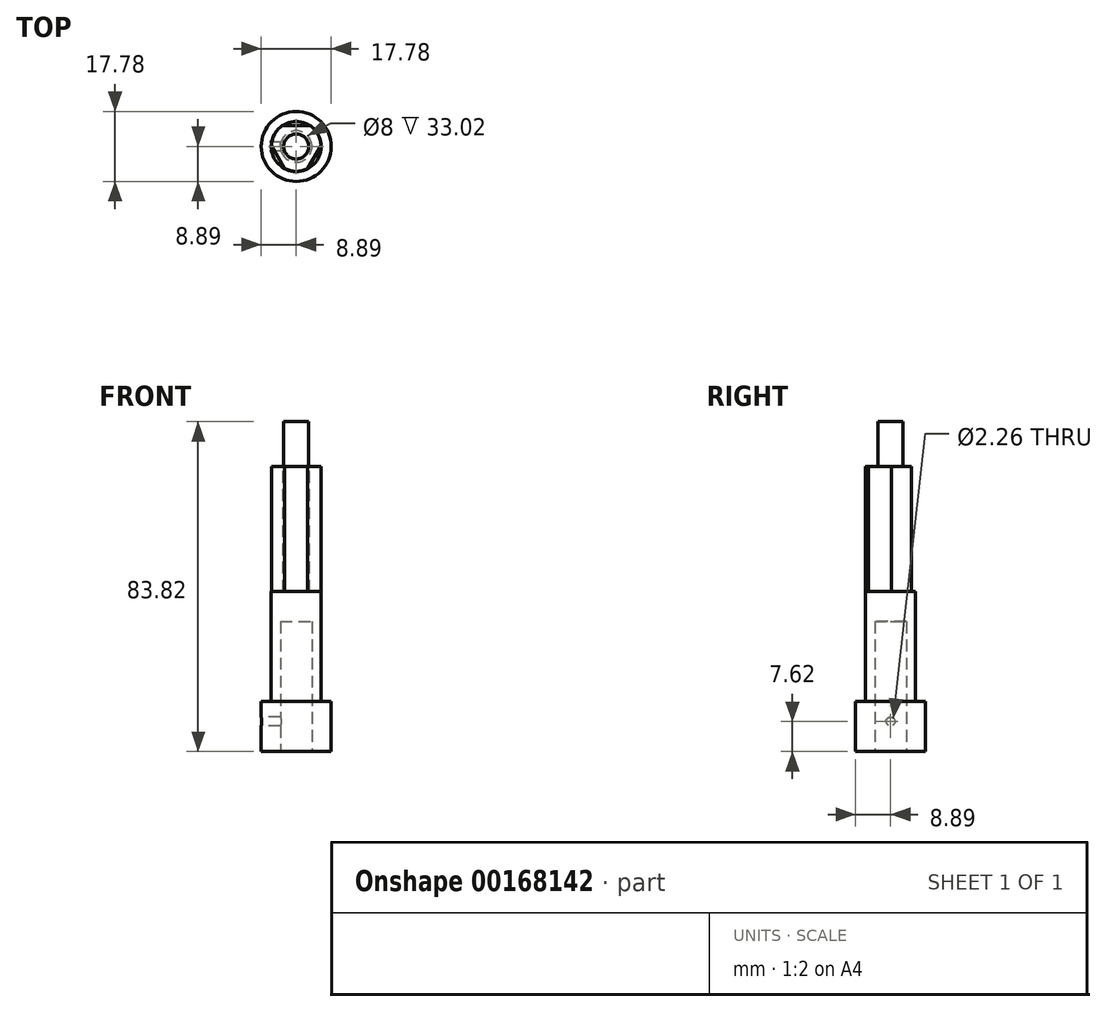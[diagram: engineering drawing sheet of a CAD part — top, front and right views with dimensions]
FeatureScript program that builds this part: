
annotation { "Feature Type Name" : "Feature", "Feature Type Description" : "" }
export const myFeature = defineFeature(function(context is Context, id is Id, definition is map)
    precondition{}
    {
        {
            var Q0;
            Q0=qCreatedBy(makeId("Top.planeOp"),FACE);
            var sketch = newSketch(context, id + "F0", { "sketchPlane" : qUnion([Q0])});
            skCircle(sketch, "E0", {"center": v(0, 0) * mm, "radius": 8.9 * mm});
            skSolve(sketch);
        }
        {
            var Q0;
            Q0=makeQuery(id+"F0.imprint","IMPRINT",FACE,{"disambiguationData":[TD([[makeQuery(id+"F0.imprint","IMPRINT",EDGE,{"derivedFrom":sQuery(id+"F0.wireOp",EDGE,"E0")}),1.0]])]});
            extrude(context, id + "F1", {"entities" : qUnion([Q0]), "depth" : 12.7 * mm});
        }
        {
            var Q0;
            Q0=makeQuery(id+"F1.opExtrude","CAP_FACE",FACE,{"disambiguationData":[OSD([sQuery(id+"F0.wireOp",EDGE,"E0")])],"isStart":false});
            var sketch = newSketch(context, id + "F2", { "sketchPlane" : qUnion([Q0])});
            skCircle(sketch, "E1", {"center": v(0, 0) * mm, "radius": 6.35 * mm});
            skSolve(sketch);
        }
        {
            var Q0;
            Q0=qSketchRegion(id+"F2",true);
            extrude(context, id + "F3", {"entities" : qUnion([Q0]), "operationType" : NewBodyOperationType.ADD, "depth" : 27.94 * mm});
        }
        {
            var Q0;
            Q0=makeQuery(id+"F3.opExtrude","CAP_FACE",FACE,{"disambiguationData":[OSD([sQuery(id+"F2.wireOp",EDGE,"E1")])],"isStart":false});
            var sketch = newSketch(context, id + "F4", { "sketchPlane" : qUnion([Q0])});
            skCircle(sketch, "E2.cCircle", {"center": v(0, 0) * mm, "radius": 5.33 * mm, "construction": true});
            skLineSegment(sketch, "E2.0", {"start": v(9.24, 5.33) * mm, "end": v(0, -10.67) * mm});
            skLineSegment(sketch, "E2.1", {"start": v(0, -10.67) * mm, "end": v(-9.24, 5.33) * mm});
            skLineSegment(sketch, "E2.2", {"start": v(-9.24, 5.33) * mm, "end": v(9.24, 5.33) * mm});
            skPoint(sketch, "E2.0.midPoint", {"position": v(4.62, -2.67) * mm});
            skSolve(sketch);
        }
        {
            var Q0;
            Q0=qSketchRegion(id+"F4",true);
            extrude(context, id + "F5", {"entities" : qUnion([Q0]), "operationType" : NewBodyOperationType.ADD, "depth" : 43.18 * mm});
        }
        {
            var Q0;
            Q0=makeQuery(id+"F5.opExtrude","CAP_FACE",FACE,{"disambiguationData":[OSD([sQuery(id+"F4.wireOp",EDGE,"E2.0"),sQuery(id+"F4.wireOp",EDGE,"E2.1"),sQuery(id+"F4.wireOp",EDGE,"E2.2")])],"isStart":false});
            var sketch = newSketch(context, id + "F6", { "sketchPlane" : qUnion([Q0])});
            skCircle(sketch, "E3", {"center": v(0, 0) * mm, "radius": 6.32 * mm});
            skCircle(sketch, "E4", {"center": v(0, 0) * mm, "radius": 20.25 * mm});
            skSolve(sketch);
        }
        {
            var Q0;
            Q0=qSketchRegion(id+"F6",true);
            var Q1;
            {var subQ0=sQuery(id+"F2.wireOp",EDGE,"E1");var subQ1=sQuery(id+"F4.wireOp",EDGE,"E2.0");Q1=makeQuery(id+"F5.boolean.opBoolean","SPLIT",FACE,{"disambiguationData":[TD([makeQuery(id+"F5.opExtrude","SWEPT_FACE",FACE,{"disambiguationData":[OSD([subQ1])]})])],"derivedFrom":makeQuery(id+"F3.opExtrude","CAP_FACE",FACE,{"disambiguationData":[OSD([subQ0])],"isStart":false})});}
            extrude(context, id + "F7", {"entities" : qUnion([Q0]), "operationType" : NewBodyOperationType.REMOVE, "endBound" : BoundingType.UP_TO_SURFACE, "oppositeDirection" : true, "endBoundEntityFace" : qUnion([Q1]), "depth" : 25.4 * mm});
        }
        {
            var Q0;
            Q0=makeQuery(id+"F1.opExtrude","CAP_FACE",FACE,{"disambiguationData":[OSD([sQuery(id+"F0.wireOp",EDGE,"E0")])],"isStart":true});
            var sketch = newSketch(context, id + "F8", { "sketchPlane" : qUnion([Q0])});
            skCircle(sketch, "E5", {"center": v(0, 0) * mm, "radius": 4 * mm});
            skSolve(sketch);
        }
        {
            var Q0;
            Q0=makeQuery(id+"F8.imprint","IMPRINT",FACE,{"disambiguationData":[TD([[makeQuery(id+"F8.imprint","IMPRINT",EDGE,{"derivedFrom":sQuery(id+"F8.wireOp",EDGE,"E5")}),1.0]])]});
            extrude(context, id + "F9", {"entities" : qUnion([Q0]), "operationType" : NewBodyOperationType.REMOVE, "oppositeDirection" : true, "depth" : 33.02 * mm});
        }
        {
            var Q0;
            Q0=makeQuery(id+"F1.opExtrude","CAP_FACE",FACE,{"disambiguationData":[OSD([sQuery(id+"F0.wireOp",EDGE,"E0")])],"isStart":false});
            var sketch = newSketch(context, id + "F10", { "sketchPlane" : qUnion([Q0])});
            skCircle(sketch, "E6.0", {"center": v(0, 0) * mm, "radius": 8.9 * mm, "construction": true});
            skPoint(sketch, "E7", {"position": v(-8.9, 0) * mm});
            skSolve(sketch);
        }
        {
            var Q0;
            Q0=sQuery(id+"F10.wireOp",VERTEX,"E7");
            var Q1;
            Q1=qCreatedBy(makeId("Right.planeOp"),FACE);
            cPlane(context, id + "F11", {"entities" : qUnion([Q0, Q1]), "cplaneType" : CPlaneType.PLANE_POINT, "offset" : 25.4 * mm, "width" : 152.4 * mm, "height" : 152.4 * mm});
        }
        {
            var Q0;
            Q0=qCreatedBy(id+"F11.planeOp",FACE);
            var sketch = newSketch(context, id + "F12", { "sketchPlane" : qUnion([Q0])});
            skLineSegment(sketch, "E8", {"start": v(0, 0) * mm, "end": v(0, 7.62) * mm, "construction": true});
            skPoint(sketch, "E9", {"position": v(0, 7.62) * mm});
            skSolve(sketch);
        }
        {
            var Q0;
            Q0=sQuery(id+"F12.wireOp",VERTEX,"E9");
            var Q1;
            Q1=makeQuery(id+"F1.opExtrude","SWEPT_BODY",BODY,{"disambiguationData":[OSD([sQuery(id+"F0.wireOp",EDGE,"E0")])]});
            hole(context, id + "F13", {"style" : HoleStyle.SIMPLE, "endStyle" : HoleEndStyle.BLIND, "oppositeDirection" : true, "standardTappedOrClearance" : lookupTablePath({ "standard" : "ANSI", "engagement" : "75%", "pitch" : "40 tpi", "size" : "#4", "type" : "Tapped" }), "standardBlindInLast" : lookupTablePath({ "standard" : "ANSI", "engagement" : "75%", "pitch" : "40 tpi", "size" : "#4", "type" : "Tapped" }), "holeDiameter" : 2.26 * mm, "holeDepth" : 8.9 * mm, "locations" : qUnion([Q0]), "scope" : qUnion([Q1]), "majorDiameter" : 2.84 * mm});
        }
        {
            var Q0;
            Q0=makeQuery(id+"F5.opExtrude","CAP_FACE",FACE,{"disambiguationData":[OSD([sQuery(id+"F4.wireOp",EDGE,"E2.0"),sQuery(id+"F4.wireOp",EDGE,"E2.1"),sQuery(id+"F4.wireOp",EDGE,"E2.2")])],"isStart":false});
            var sketch = newSketch(context, id + "F14", { "sketchPlane" : qUnion([Q0])});
            skCircle(sketch, "E10", {"center": v(0, 0) * mm, "radius": 3.18 * mm});
            skCircle(sketch, "E11", {"center": v(0, 0) * mm, "radius": 8.9 * mm});
            skSolve(sketch);
        }
        {
            var Q0;
            Q0=qSketchRegion(id+"F14",true);
            extrude(context, id + "F15", {"entities" : qUnion([Q0]), "operationType" : NewBodyOperationType.REMOVE, "oppositeDirection" : true, "depth" : 11.43 * mm});
        }
    });
